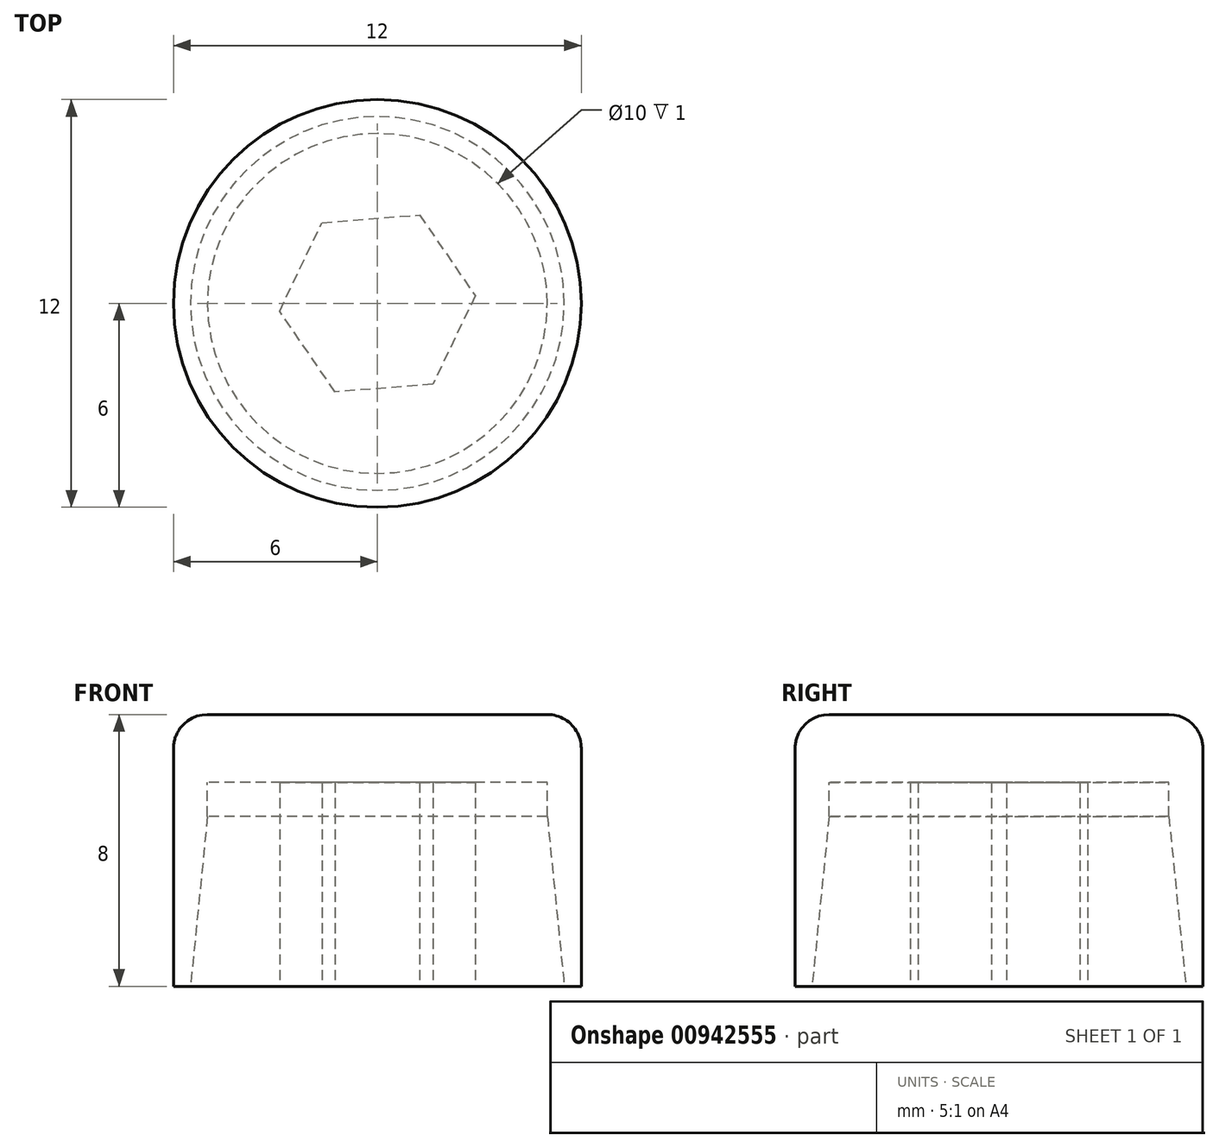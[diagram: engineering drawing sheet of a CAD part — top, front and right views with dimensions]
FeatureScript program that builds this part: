
annotation { "Feature Type Name" : "Feature", "Feature Type Description" : "" }
export const myFeature = defineFeature(function(context is Context, id is Id, definition is map)
    precondition{}
    {
        {
            var Q0;
            Q0=qCreatedBy(makeId("Top.planeOp"),FACE);
            var sketch = newSketch(context, id + "F0", { "sketchPlane" : qUnion([Q0])});
            skCircle(sketch, "E0.cCircle", {"center": v(0, 0) * mm, "radius": 2.5 * mm, "construction": true});
            skLineSegment(sketch, "E0.0", {"start": v(2.88, 0.22) * mm, "end": v(1.63, -2.38) * mm});
            skLineSegment(sketch, "E0.1", {"start": v(1.63, -2.38) * mm, "end": v(-1.24, -2.6) * mm});
            skLineSegment(sketch, "E0.2", {"start": v(-1.24, -2.6) * mm, "end": v(-2.88, -0.22) * mm});
            skLineSegment(sketch, "E0.3", {"start": v(-2.88, -0.22) * mm, "end": v(-1.63, 2.38) * mm});
            skLineSegment(sketch, "E0.4", {"start": v(-1.63, 2.38) * mm, "end": v(1.24, 2.6) * mm});
            skLineSegment(sketch, "E0.5", {"start": v(1.24, 2.6) * mm, "end": v(2.88, 0.22) * mm});
            skPoint(sketch, "E0.0.midPoint", {"position": v(2.26, -1.08) * mm});
            skSolve(sketch);
        }
        {
            var Q0;
            Q0=makeQuery(id+"F0.imprint","IMPRINT",FACE,{"disambiguationData":[TD([[makeQuery(id+"F0.imprint","IMPRINT",EDGE,{"derivedFrom":sQuery(id+"F0.wireOp",EDGE,"E0.0")}),-1.0]])]});
            extrude(context, id + "F1", {"entities" : qUnion([Q0]), "depth" : 6 * mm, "offsetDistance" : 25 * mm});
        }
        {
            var Q0;
            Q0=makeQuery(id+"F1.opExtrude","CAP_FACE",FACE,{"disambiguationData":[OSD([sQuery(id+"F0.wireOp",EDGE,"E0.0"),sQuery(id+"F0.wireOp",EDGE,"E0.1"),sQuery(id+"F0.wireOp",EDGE,"E0.2"),sQuery(id+"F0.wireOp",EDGE,"E0.3"),sQuery(id+"F0.wireOp",EDGE,"E0.4"),sQuery(id+"F0.wireOp",EDGE,"E0.5")])],"isStart":false});
            var sketch = newSketch(context, id + "F2", { "sketchPlane" : qUnion([Q0])});
            skCircle(sketch, "E1", {"center": v(0, 0) * mm, "radius": 5 * mm});
            skSolve(sketch);
        }
        {
            var Q0;
            Q0=makeQuery(id+"F2.imprint","IMPRINT",FACE,{"disambiguationData":[TD([[makeQuery(id+"F2.imprint","IMPRINT",EDGE,{"derivedFrom":sQuery(id+"F2.wireOp",EDGE,"E1")}),1.0]])]});
            var Q1;
            Q1=makeQuery(id+"F2.imprint","IMPRINT",FACE,{"disambiguationData":[TD([[makeQuery(id+"F2.imprint","IMPRINT",EDGE,{"derivedFrom":makeQuery(id+"F1.opExtrude","CAP_EDGE",EDGE,{"disambiguationData":[OSD([sQuery(id+"F0.wireOp",EDGE,"E0.0")])],"isStart":false})}),-1.0]])]});
            extrude(context, id + "F3", {"entities" : qUnion([Q0, Q1]), "operationType" : NewBodyOperationType.ADD, "depth" : 2 * mm, "offsetDistance" : 25 * mm});
        }
        {
            var Q0;
            Q0=makeQuery(id+"F3.opExtrude","CAP_FACE",FACE,{"disambiguationData":[OSD([sQuery(id+"F2.wireOp",EDGE,"E1")])],"isStart":false});
            var sketch = newSketch(context, id + "F4", { "sketchPlane" : qUnion([Q0])});
            skCircle(sketch, "E2.0", {"center": v(0, 0) * mm, "radius": 6 * mm});
            skSolve(sketch);
        }
        {
            var Q0;
            Q0=makeQuery(id+"F4.imprint","IMPRINT",FACE,{"disambiguationData":[TD([[makeQuery(id+"F4.imprint","IMPRINT",EDGE,{"derivedFrom":sQuery(id+"F4.wireOp",EDGE,"E2.0")}),1.0]])]});
            extrude(context, id + "F5", {"entities" : qUnion([Q0]), "operationType" : NewBodyOperationType.ADD, "oppositeDirection" : true, "depth" : 8 * mm, "offsetDistance" : 25 * mm});
        }
        {
            var Q0;
            Q0=makeQuery(id+"F5.opExtrude","CAP_EDGE",EDGE,{"disambiguationData":[OSD([sQuery(id+"F4.wireOp",EDGE,"E2.0")])],"isStart":true});
            fillet(context, id + "F6", {"entities" : qUnion([Q0]), "radius" : 1 * mm, "tangentPropagation" : true, "allowEdgeOverflow" : false});
        }
        {
            var Q0;
            Q0=makeQuery(id+"F5.opExtrude","CAP_EDGE",EDGE,{"disambiguationData":[OSD([sQuery(id+"F2.wireOp",EDGE,"E1")])],"isStart":false});
            chamfer(context, id + "F7", {"entities" : qUnion([Q0]), "chamferType" : ChamferType.TWO_OFFSETS, "width1" : 0.5 * mm, "oppositeDirection" : false, "width2" : 5 * mm, "tangentPropagation" : true});
        }
    });
